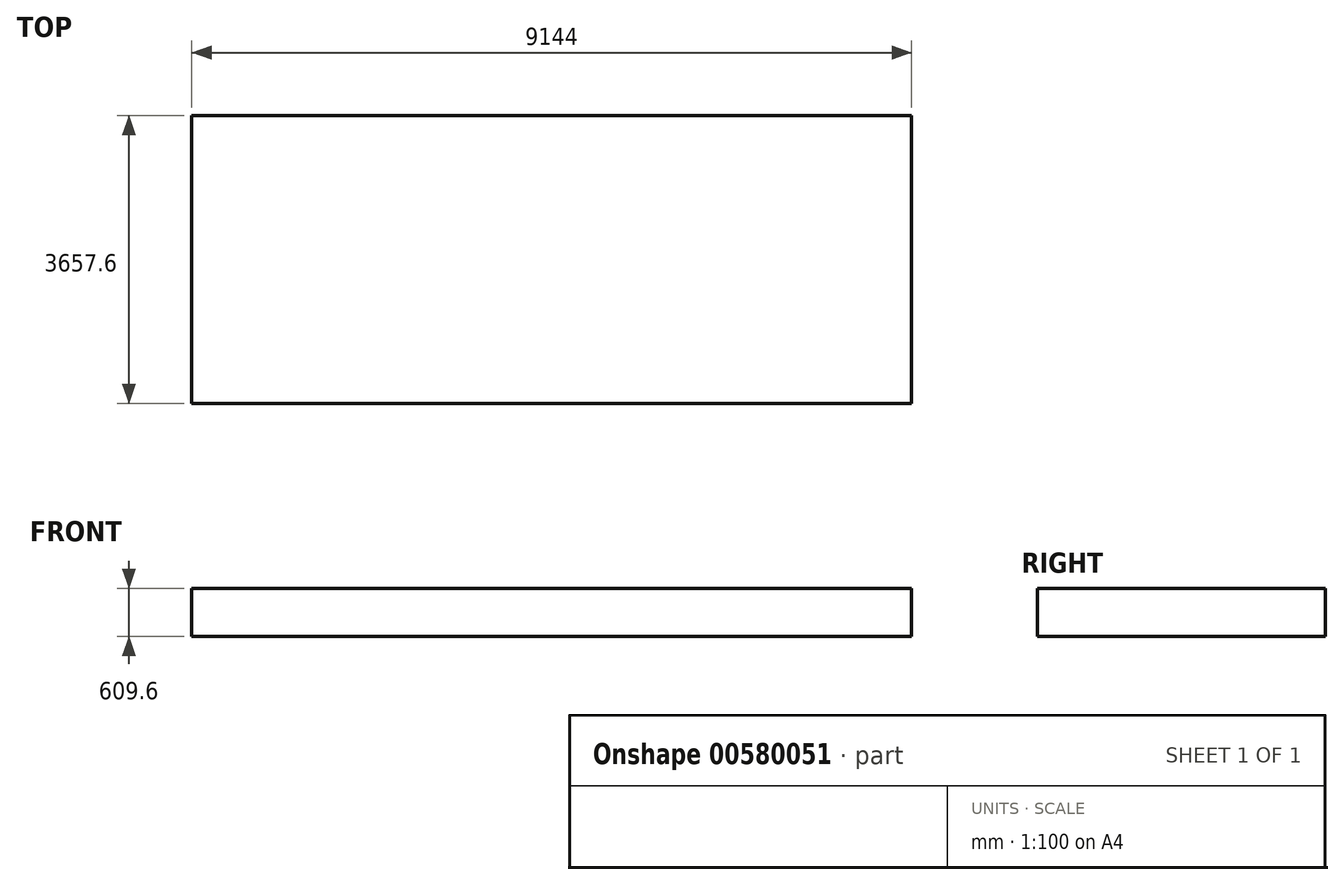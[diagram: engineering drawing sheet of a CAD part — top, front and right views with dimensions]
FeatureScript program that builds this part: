
annotation { "Feature Type Name" : "Feature", "Feature Type Description" : "" }
export const myFeature = defineFeature(function(context is Context, id is Id, definition is map)
    precondition{}
    {
        {
            var Q0;
            Q0=qCreatedBy(makeId("Top.planeOp"),FACE);
            var sketch = newSketch(context, id + "F0", { "sketchPlane" : qUnion([Q0])});
            skLineSegment(sketch, "E0.bottom", {"start": v(-4579.91, 846.41) * mm, "end": v(4564.09, 846.41) * mm});
            skLineSegment(sketch, "E0.top", {"start": v(-4579.91, -2811.19) * mm, "end": v(4564.09, -2811.19) * mm});
            skLineSegment(sketch, "E0.left", {"start": v(-4579.91, 846.41) * mm, "end": v(-4579.91, -2811.19) * mm});
            skLineSegment(sketch, "E0.right", {"start": v(4564.09, 846.41) * mm, "end": v(4564.09, -2811.19) * mm});
            skSolve(sketch);
        }
        {
            var Q0;
            Q0 = qSketchRegion(id + "F0", true);
            extrude(context, id + "F1", {"entities" : qUnion([Q0]), "depth" : 609.6 * mm, "offsetDistance" : 30.48 * mm});
        }
    });
